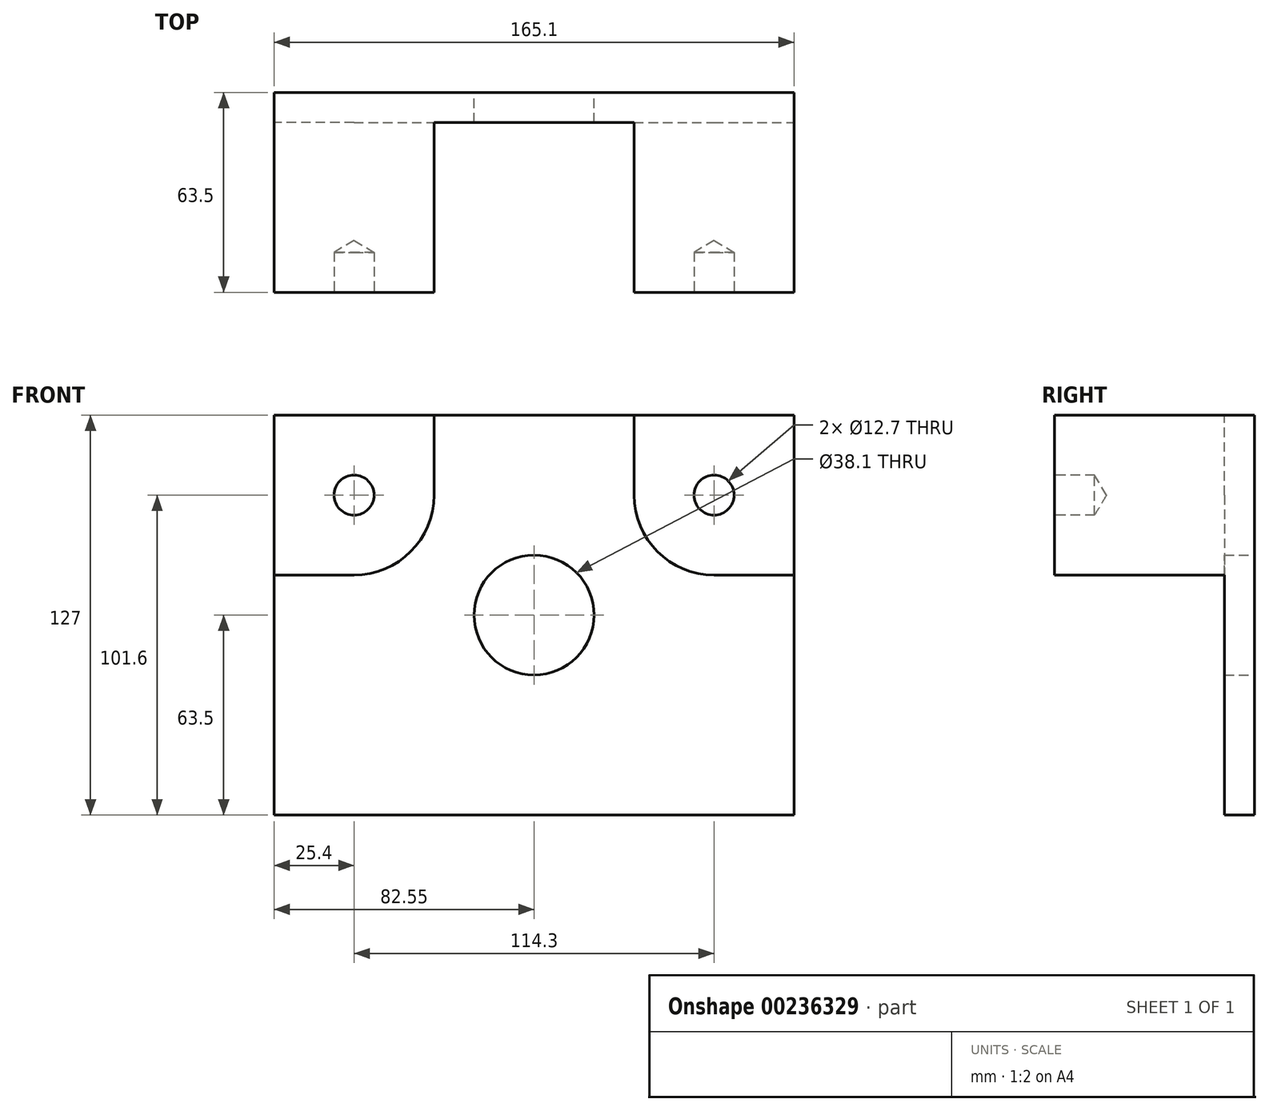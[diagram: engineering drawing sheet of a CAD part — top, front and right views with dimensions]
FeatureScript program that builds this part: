
annotation { "Feature Type Name" : "Feature", "Feature Type Description" : "" }
export const myFeature = defineFeature(function(context is Context, id is Id, definition is map)
    precondition{}
    {
        {
            var Q0;
            Q0=qCreatedBy(makeId("Front.planeOp"),FACE);
            var sketch = newSketch(context, id + "F0", { "sketchPlane" : qUnion([Q0])});
            skLineSegment(sketch, "E0.bottom", {"start": v(82.55, 63.5) * mm, "end": v(-82.55, 63.5) * mm});
            skLineSegment(sketch, "E0.top", {"start": v(82.55, -63.5) * mm, "end": v(-82.55, -63.5) * mm});
            skLineSegment(sketch, "E0.left", {"start": v(82.55, 63.5) * mm, "end": v(82.55, -63.5) * mm});
            skLineSegment(sketch, "E0.right", {"start": v(-82.55, 63.5) * mm, "end": v(-82.55, -63.5) * mm});
            skPoint(sketch, "E0.middle", {"position": v(0, 0) * mm});
            skSolve(sketch);
        }
        {
            var Q0;
            Q0=qCreatedBy(makeId("Front.planeOp"),FACE);
            var sketch = newSketch(context, id + "F1", { "sketchPlane" : qUnion([Q0])});
            skCircle(sketch, "E1", {"center": v(0, 0) * mm, "radius": 19.1 * mm});
            skSolve(sketch);
        }
        {
            var Q0;
            Q0=makeQuery(id+"F0.imprint","IMPRINT",FACE,{"disambiguationData":[TD([[makeQuery(id+"F0.imprint","IMPRINT",EDGE,{"derivedFrom":sQuery(id+"F0.wireOp",EDGE,"E0.bottom")}),1.0]])]});
            extrude(context, id + "F2", {"entities" : qUnion([Q0]), "depth" : 9.52 * mm});
        }
        {
            var Q0;
            Q0=sQuery(id+"F1.wireOp",VERTEX,"E1.center");
            var Q1;
            Q1=makeQuery(id+"F2.opExtrude","SWEPT_BODY",BODY,{"disambiguationData":[OSD([sQuery(id+"F0.wireOp",EDGE,"E0.bottom"),sQuery(id+"F0.wireOp",EDGE,"E0.top"),sQuery(id+"F0.wireOp",EDGE,"E0.left"),sQuery(id+"F0.wireOp",EDGE,"E0.right")])]});
            hole(context, id + "F3", {"style" : HoleStyle.SIMPLE, "endStyle" : HoleEndStyle.THROUGH, "oppositeDirection" : true, "holeDiameter" : 38.1 * mm, "locations" : qUnion([Q0]), "scope" : qUnion([Q1]), "isTappedThrough" : true});
        }
        {
            var Q0;
            Q0=qCreatedBy(makeId("Front.planeOp"),FACE);
            var sketch = newSketch(context, id + "F4", { "sketchPlane" : qUnion([Q0])});
            skLineSegment(sketch, "E2.bottom", {"start": v(-82.55, 63.5) * mm, "end": v(-31.75, 63.5) * mm});
            skLineSegment(sketch, "E2.top", {"start": v(-82.55, 12.7) * mm, "end": v(-31.75, 12.7) * mm});
            skLineSegment(sketch, "E2.left", {"start": v(-82.55, 63.5) * mm, "end": v(-82.55, 12.7) * mm});
            skLineSegment(sketch, "E2.right", {"start": v(-31.75, 63.5) * mm, "end": v(-31.75, 12.7) * mm});
            skLineSegment(sketch, "E3.bottom", {"start": v(82.55, 63.5) * mm, "end": v(31.75, 63.5) * mm});
            skLineSegment(sketch, "E3.top", {"start": v(82.55, 12.7) * mm, "end": v(31.75, 12.7) * mm});
            skLineSegment(sketch, "E3.left", {"start": v(82.55, 63.5) * mm, "end": v(82.55, 12.7) * mm});
            skLineSegment(sketch, "E3.right", {"start": v(31.75, 63.5) * mm, "end": v(31.75, 12.7) * mm});
            skSolve(sketch);
        }
        {
            var Q0;
            Q0 = qSketchRegion(id + "F4", true);
            extrude(context, id + "F5", {"entities" : qUnion([Q0]), "operationType" : NewBodyOperationType.ADD, "depth" : 63.5 * mm});
        }
        {
            var Q0;
            Q0=makeQuery(id+"F5.opExtrude","SWEPT_EDGE",EDGE,{"disambiguationData":[OSD([sQuery(id+"F4.wireOp",EDGE,"E2.top"),sQuery(id+"F4.wireOp",EDGE,"E2.right")])]});
            var Q1;
            Q1=makeQuery(id+"F5.opExtrude","SWEPT_EDGE",EDGE,{"disambiguationData":[OSD([sQuery(id+"F4.wireOp",EDGE,"E3.top"),sQuery(id+"F4.wireOp",EDGE,"E3.right")])]});
            fillet(context, id + "F6", {"entities" : qUnion([Q0, Q1]), "radius" : 25.4 * mm, "tangentPropagation" : true, "allowEdgeOverflow" : false});
        }
        {
            var Q0;
            Q0=makeQuery(id+"F5.opExtrude","CAP_FACE",FACE,{"disambiguationData":[OSD([sQuery(id+"F4.wireOp",EDGE,"E2.bottom"),sQuery(id+"F4.wireOp",EDGE,"E2.top"),sQuery(id+"F4.wireOp",EDGE,"E2.left"),sQuery(id+"F4.wireOp",EDGE,"E2.right")])],"isStart":false});
            var sketch = newSketch(context, id + "F7", { "sketchPlane" : qUnion([Q0])});
            skPoint(sketch, "E4", {"position": v(-57.15, 38.1) * mm});
            skPoint(sketch, "E5", {"position": v(57.15, 38.1) * mm});
            skSolve(sketch);
        }
        {
            var Q0;
            Q0=sQuery(id+"F7.wireOp",VERTEX,"E4");
            var Q1;
            Q1=sQuery(id+"F7.wireOp",VERTEX,"E5");
            var Q2;
            Q2=makeQuery(id+"F2.opExtrude","SWEPT_BODY",BODY,{"disambiguationData":[OSD([sQuery(id+"F0.wireOp",EDGE,"E0.bottom"),sQuery(id+"F0.wireOp",EDGE,"E0.top"),sQuery(id+"F0.wireOp",EDGE,"E0.left"),sQuery(id+"F0.wireOp",EDGE,"E0.right")])]});
            hole(context, id + "F8", {"style" : HoleStyle.SIMPLE, "endStyle" : HoleEndStyle.BLIND, "holeDiameter" : 12.7 * mm, "holeDepth" : 12.7 * mm, "locations" : qUnion([Q0, Q1]), "scope" : qUnion([Q2])});
        }
    });
